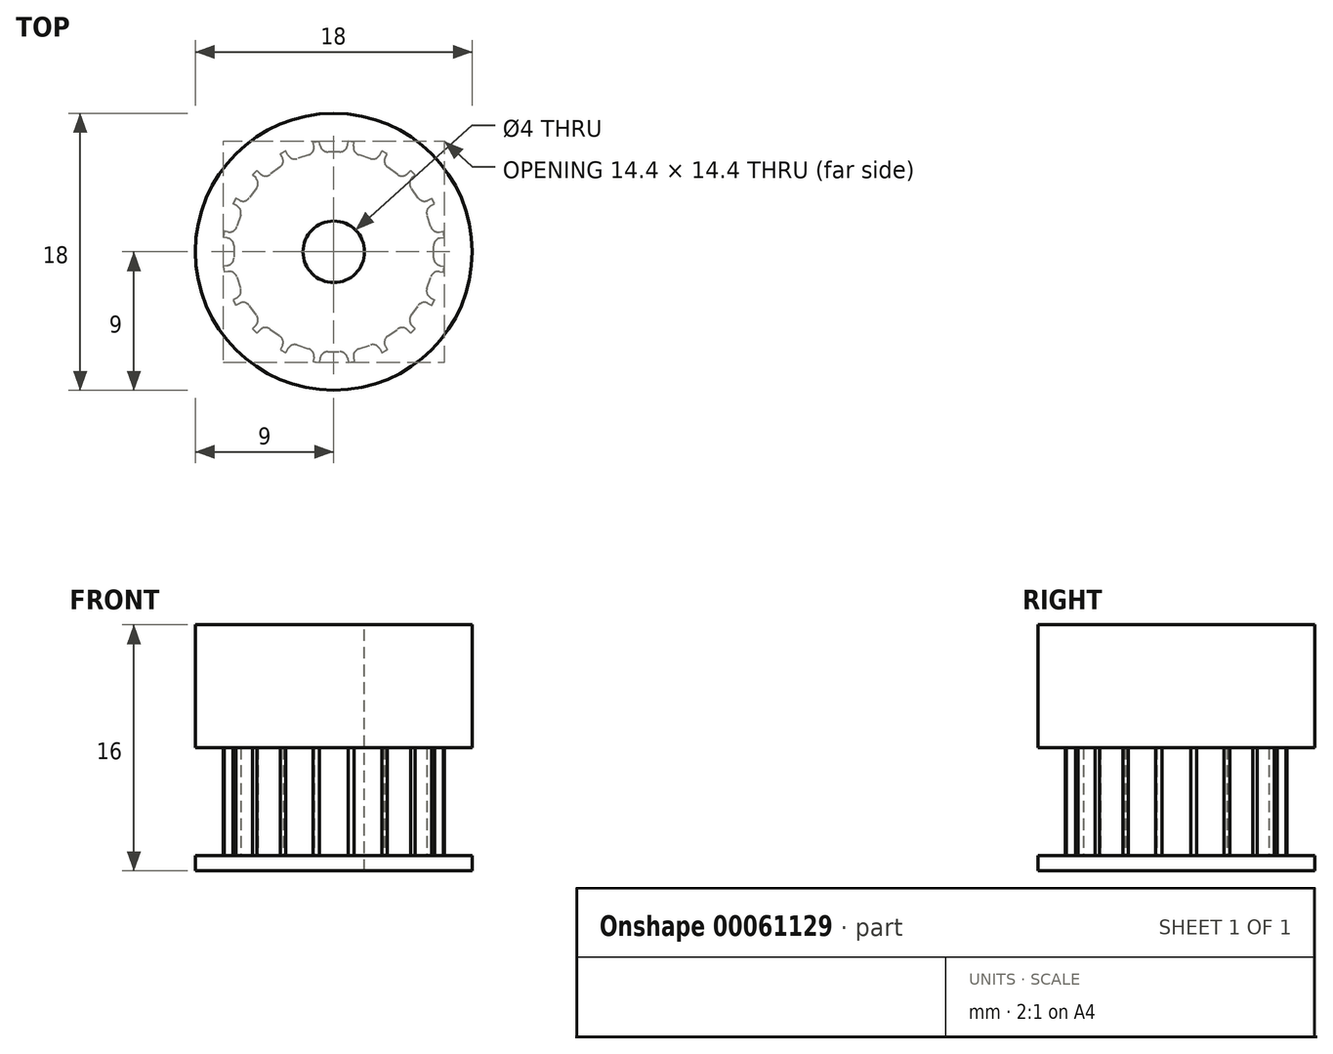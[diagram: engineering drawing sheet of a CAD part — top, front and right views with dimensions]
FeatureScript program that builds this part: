
annotation { "Feature Type Name" : "Feature", "Feature Type Description" : "" }
export const myFeature = defineFeature(function(context is Context, id is Id, definition is map)
    precondition{}
    {
        {
            var Q0;
            Q0=qCreatedBy(makeId("Top.planeOp"),FACE);
            var sketch = newSketch(context, id + "F0", { "sketchPlane" : qUnion([Q0])});
            skCircle(sketch, "E0", {"center": v(0, 0) * mm, "radius": 6.5 * mm, "construction": true});
            skLineSegment(sketch, "E1", {"start": v(0, 0) * mm, "end": v(0, 6.5) * mm, "construction": true});
            skLineSegment(sketch, "E2", {"start": v(0, 0) * mm, "end": v(-1.14, 7.17) * mm});
            skCircle(sketch, "E3", {"center": v(0, 0) * mm, "radius": 7.26 * mm, "construction": true});
            skLineSegment(sketch, "E4", {"start": v(-0.4, 6.5) * mm, "end": v(0, 6.5) * mm});
            skLineSegment(sketch, "E5.0", {"start": v(-0.9, 6.92) * mm, "end": v(-0.94, 7.2) * mm});
            skLineSegment(sketch, "E6.MirrorCS", {"start": v(0.82, 6.45) * mm, "end": v(0.83, 6.5) * mm});
            skPoint(sketch, "E7.newPointB", {"position": v(-0.82, 6.45) * mm});
            skArc(sketch, "E7.filletArc", {"start": v(-0.9, 6.92) * mm, "mid": v(-0.72, 6.62) * mm, "end": v(-0.4, 6.5) * mm});
            skLineSegment(sketch, "E8", {"start": v(-1.14, 7.17) * mm, "end": v(-0.94, 7.2) * mm});
            skPoint(sketch, "E9.MirrorCS.end.orphan", {"position": v(1.14, 7.17) * mm});
            skLineSegment(sketch, "E10.trimOffspring", {"start": v(0.94, 7.2) * mm, "end": v(0.94, 7.2) * mm});
            skLineSegment(sketch, "E11.MirrorCS", {"start": v(0, 0) * mm, "end": v(1.14, 7.17) * mm});
            skLineSegment(sketch, "E12.MirrorCS", {"start": v(0.9, 6.92) * mm, "end": v(0.94, 7.2) * mm});
            skArc(sketch, "E13.MirrorCS", {"start": v(0.9, 6.92) * mm, "mid": v(0.72, 6.62) * mm, "end": v(0.4, 6.5) * mm});
            skLineSegment(sketch, "E14.MirrorCS", {"start": v(0.4, 6.5) * mm, "end": v(0, 6.5) * mm});
            skLineSegment(sketch, "E15.MirrorCS", {"start": v(1.14, 7.17) * mm, "end": v(0.94, 7.2) * mm});
            skSolve(sketch);
        }
        {
            var Q0;
            Q0=makeQuery(id+"F0.imprint","IMPRINT",FACE,{"disambiguationData":[TD([[makeQuery(id+"F0.imprint","IMPRINT",EDGE,{"derivedFrom":sQuery(id+"F0.wireOp",EDGE,"E2")}),-1.0]])]});
            extrude(context, id + "F1", {"entities" : qUnion([Q0]), "endBound" : BoundingType.SYMMETRIC, "depth" : 7 * mm});
        }
        {
            var Q0;
            Q0=makeQuery(id+"F1.opExtrude","SWEPT_BODY",BODY,{"disambiguationData":[OSD([sQuery(id+"F0.wireOp",EDGE,"E2"),sQuery(id+"F0.wireOp",EDGE,"E4"),sQuery(id+"F0.wireOp",EDGE,"E5.0"),sQuery(id+"F0.wireOp",EDGE,"E7.filletArc"),sQuery(id+"F0.wireOp",EDGE,"E8"),sQuery(id+"F0.wireOp",EDGE,"E11.MirrorCS"),sQuery(id+"F0.wireOp",EDGE,"E12.MirrorCS"),sQuery(id+"F0.wireOp",EDGE,"E13.MirrorCS"),sQuery(id+"F0.wireOp",EDGE,"E14.MirrorCS"),sQuery(id+"F0.wireOp",EDGE,"E15.MirrorCS")])]});
            var Q1;
            Q1=makeQuery(id+"F1.opExtrude","SWEPT_EDGE",EDGE,{"disambiguationData":[OSD([sQuery(id+"F0.wireOp",EDGE,"E2"),sQuery(id+"F0.wireOp",EDGE,"E11.MirrorCS")])]});
            circularPattern(context, id + "F2", {"operationType" : NewBodyOperationType.ADD, "entities" : qUnion([Q0]), "axis" : qUnion([Q1]), "angle" : 360 * degree, "instanceCount" : 20, "equalSpace" : true});
        }
        {
            var Q0;
            {var subQ0=makeQuery(id+"F1.opExtrude","CAP_FACE",FACE,{"disambiguationData":[OSD([sQuery(id+"F0.wireOp",EDGE,"E2"),sQuery(id+"F0.wireOp",EDGE,"E4"),sQuery(id+"F0.wireOp",EDGE,"E5.0"),sQuery(id+"F0.wireOp",EDGE,"E7.filletArc"),sQuery(id+"F0.wireOp",EDGE,"E8"),sQuery(id+"F0.wireOp",EDGE,"E11.MirrorCS"),sQuery(id+"F0.wireOp",EDGE,"E12.MirrorCS"),sQuery(id+"F0.wireOp",EDGE,"E13.MirrorCS"),sQuery(id+"F0.wireOp",EDGE,"E14.MirrorCS"),sQuery(id+"F0.wireOp",EDGE,"E15.MirrorCS")])],"isStart":true});Q0=makeQuery(id+"F2.boolean.opBoolean","MERGE",FACE,{"derivedFrom":[subQ0,makeQuery(id+"F2.opPattern","COPY",FACE,{"derivedFrom":subQ0,"instanceName":"1"}),makeQuery(id+"F2.opPattern","COPY",FACE,{"derivedFrom":subQ0,"instanceName":"2"}),makeQuery(id+"F2.opPattern","COPY",FACE,{"derivedFrom":subQ0,"instanceName":"3"}),makeQuery(id+"F2.opPattern","COPY",FACE,{"derivedFrom":subQ0,"instanceName":"4"}),makeQuery(id+"F2.opPattern","COPY",FACE,{"derivedFrom":subQ0,"instanceName":"5"}),makeQuery(id+"F2.opPattern","COPY",FACE,{"derivedFrom":subQ0,"instanceName":"6"}),makeQuery(id+"F2.opPattern","COPY",FACE,{"derivedFrom":subQ0,"instanceName":"7"}),makeQuery(id+"F2.opPattern","COPY",FACE,{"derivedFrom":subQ0,"instanceName":"8"}),makeQuery(id+"F2.opPattern","COPY",FACE,{"derivedFrom":subQ0,"instanceName":"9"}),makeQuery(id+"F2.opPattern","COPY",FACE,{"derivedFrom":subQ0,"instanceName":"10"}),makeQuery(id+"F2.opPattern","COPY",FACE,{"derivedFrom":subQ0,"instanceName":"11"}),makeQuery(id+"F2.opPattern","COPY",FACE,{"derivedFrom":subQ0,"instanceName":"12"}),makeQuery(id+"F2.opPattern","COPY",FACE,{"derivedFrom":subQ0,"instanceName":"13"}),makeQuery(id+"F2.opPattern","COPY",FACE,{"derivedFrom":subQ0,"instanceName":"14"}),makeQuery(id+"F2.opPattern","COPY",FACE,{"derivedFrom":subQ0,"instanceName":"15"}),makeQuery(id+"F2.opPattern","COPY",FACE,{"derivedFrom":subQ0,"instanceName":"16"}),makeQuery(id+"F2.opPattern","COPY",FACE,{"derivedFrom":subQ0,"instanceName":"17"}),makeQuery(id+"F2.opPattern","COPY",FACE,{"derivedFrom":subQ0,"instanceName":"18"}),makeQuery(id+"F2.opPattern","COPY",FACE,{"derivedFrom":subQ0,"instanceName":"19"})]});}
            var sketch = newSketch(context, id + "F3", { "sketchPlane" : qUnion([Q0])});
            skCircle(sketch, "E16", {"center": v(0, 0) * mm, "radius": 9 * mm});
            skSolve(sketch);
        }
        {
            var Q0;
            Q0=makeQuery(id+"F3.imprint","IMPRINT",FACE,{"disambiguationData":[TD([[makeQuery(id+"F3.imprint","IMPRINT",EDGE,{"derivedFrom":sQuery(id+"F3.wireOp",EDGE,"E16")}),1.0]])]});
            var Q1;
            {var subQ2=makeQuery(id+"F1.opExtrude","CAP_EDGE",EDGE,{"disambiguationData":[OSD([sQuery(id+"F0.wireOp",EDGE,"E5.0")])],"isStart":true});Q1=makeQuery(id+"F3.imprint","IMPRINT",FACE,{"disambiguationData":[TD([[makeQuery(id+"F3.imprint","IMPRINT",EDGE,{"derivedFrom":subQ2}),-1.0]])]});}
            extrude(context, id + "F4", {"entities" : qUnion([Q0, Q1]), "operationType" : NewBodyOperationType.ADD, "depth" : 1 * mm});
        }
        {
            var Q0;
            {var subQ0=makeQuery(id+"F1.opExtrude","CAP_FACE",FACE,{"disambiguationData":[OSD([sQuery(id+"F0.wireOp",EDGE,"E2"),sQuery(id+"F0.wireOp",EDGE,"E4"),sQuery(id+"F0.wireOp",EDGE,"E5.0"),sQuery(id+"F0.wireOp",EDGE,"E7.filletArc"),sQuery(id+"F0.wireOp",EDGE,"E8"),sQuery(id+"F0.wireOp",EDGE,"E11.MirrorCS"),sQuery(id+"F0.wireOp",EDGE,"E12.MirrorCS"),sQuery(id+"F0.wireOp",EDGE,"E13.MirrorCS"),sQuery(id+"F0.wireOp",EDGE,"E14.MirrorCS"),sQuery(id+"F0.wireOp",EDGE,"E15.MirrorCS")])],"isStart":false});Q0=makeQuery(id+"F2.boolean.opBoolean","MERGE",FACE,{"derivedFrom":[subQ0,makeQuery(id+"F2.opPattern","COPY",FACE,{"derivedFrom":subQ0,"instanceName":"1"}),makeQuery(id+"F2.opPattern","COPY",FACE,{"derivedFrom":subQ0,"instanceName":"2"}),makeQuery(id+"F2.opPattern","COPY",FACE,{"derivedFrom":subQ0,"instanceName":"3"}),makeQuery(id+"F2.opPattern","COPY",FACE,{"derivedFrom":subQ0,"instanceName":"4"}),makeQuery(id+"F2.opPattern","COPY",FACE,{"derivedFrom":subQ0,"instanceName":"5"}),makeQuery(id+"F2.opPattern","COPY",FACE,{"derivedFrom":subQ0,"instanceName":"6"}),makeQuery(id+"F2.opPattern","COPY",FACE,{"derivedFrom":subQ0,"instanceName":"7"}),makeQuery(id+"F2.opPattern","COPY",FACE,{"derivedFrom":subQ0,"instanceName":"8"}),makeQuery(id+"F2.opPattern","COPY",FACE,{"derivedFrom":subQ0,"instanceName":"9"}),makeQuery(id+"F2.opPattern","COPY",FACE,{"derivedFrom":subQ0,"instanceName":"10"}),makeQuery(id+"F2.opPattern","COPY",FACE,{"derivedFrom":subQ0,"instanceName":"11"}),makeQuery(id+"F2.opPattern","COPY",FACE,{"derivedFrom":subQ0,"instanceName":"12"}),makeQuery(id+"F2.opPattern","COPY",FACE,{"derivedFrom":subQ0,"instanceName":"13"}),makeQuery(id+"F2.opPattern","COPY",FACE,{"derivedFrom":subQ0,"instanceName":"14"}),makeQuery(id+"F2.opPattern","COPY",FACE,{"derivedFrom":subQ0,"instanceName":"15"}),makeQuery(id+"F2.opPattern","COPY",FACE,{"derivedFrom":subQ0,"instanceName":"16"}),makeQuery(id+"F2.opPattern","COPY",FACE,{"derivedFrom":subQ0,"instanceName":"17"}),makeQuery(id+"F2.opPattern","COPY",FACE,{"derivedFrom":subQ0,"instanceName":"18"}),makeQuery(id+"F2.opPattern","COPY",FACE,{"derivedFrom":subQ0,"instanceName":"19"})]});}
            var sketch = newSketch(context, id + "F5", { "sketchPlane" : qUnion([Q0])});
            skCircle(sketch, "E17.0", {"center": v(0, 0) * mm, "radius": 9 * mm});
            skSolve(sketch);
        }
        {
            var Q0;
            Q0=makeQuery(id+"F5.imprint","IMPRINT",FACE,{"disambiguationData":[TD([[makeQuery(id+"F5.imprint","IMPRINT",EDGE,{"derivedFrom":sQuery(id+"F5.wireOp",EDGE,"E17.0")}),1.0]])]});
            var Q1;
            {var subQ3=makeQuery(id+"F1.opExtrude","CAP_EDGE",EDGE,{"disambiguationData":[OSD([sQuery(id+"F0.wireOp",EDGE,"E5.0")])],"isStart":false});Q1=makeQuery(id+"F5.imprint","IMPRINT",FACE,{"disambiguationData":[TD([[makeQuery(id+"F5.imprint","IMPRINT",EDGE,{"derivedFrom":subQ3}),1.0]])]});}
            extrude(context, id + "F6", {"entities" : qUnion([Q0, Q1]), "operationType" : NewBodyOperationType.ADD, "depth" : 8 * mm});
        }
        {
            var Q0;
            Q0=makeQuery(id+"F6.opExtrude","CAP_FACE",FACE,{"disambiguationData":[OSD([sQuery(id+"F5.wireOp",EDGE,"E17.0")])],"isStart":false});
            var sketch = newSketch(context, id + "F7", { "sketchPlane" : qUnion([Q0])});
            skPoint(sketch, "E18", {"position": v(0, 0) * mm});
            skSolve(sketch);
        }
        {
            var Q0;
            Q0=sQuery(id+"F7.wireOp",VERTEX,"E18");
            var Q1;
            Q1=makeQuery(id+"F1.opExtrude","SWEPT_BODY",BODY,{"disambiguationData":[OSD([sQuery(id+"F0.wireOp",EDGE,"E2"),sQuery(id+"F0.wireOp",EDGE,"E4"),sQuery(id+"F0.wireOp",EDGE,"E5.0"),sQuery(id+"F0.wireOp",EDGE,"E7.filletArc"),sQuery(id+"F0.wireOp",EDGE,"E8"),sQuery(id+"F0.wireOp",EDGE,"E11.MirrorCS"),sQuery(id+"F0.wireOp",EDGE,"E12.MirrorCS"),sQuery(id+"F0.wireOp",EDGE,"E13.MirrorCS"),sQuery(id+"F0.wireOp",EDGE,"E14.MirrorCS"),sQuery(id+"F0.wireOp",EDGE,"E15.MirrorCS")])]});
            hole(context, id + "F8", {"style" : HoleStyle.SIMPLE, "holeDiameter" : 4 * mm, "endStyle" : HoleEndStyle.THROUGH, "locations" : qUnion([Q0]), "scope" : qUnion([Q1])});
        }
    });
